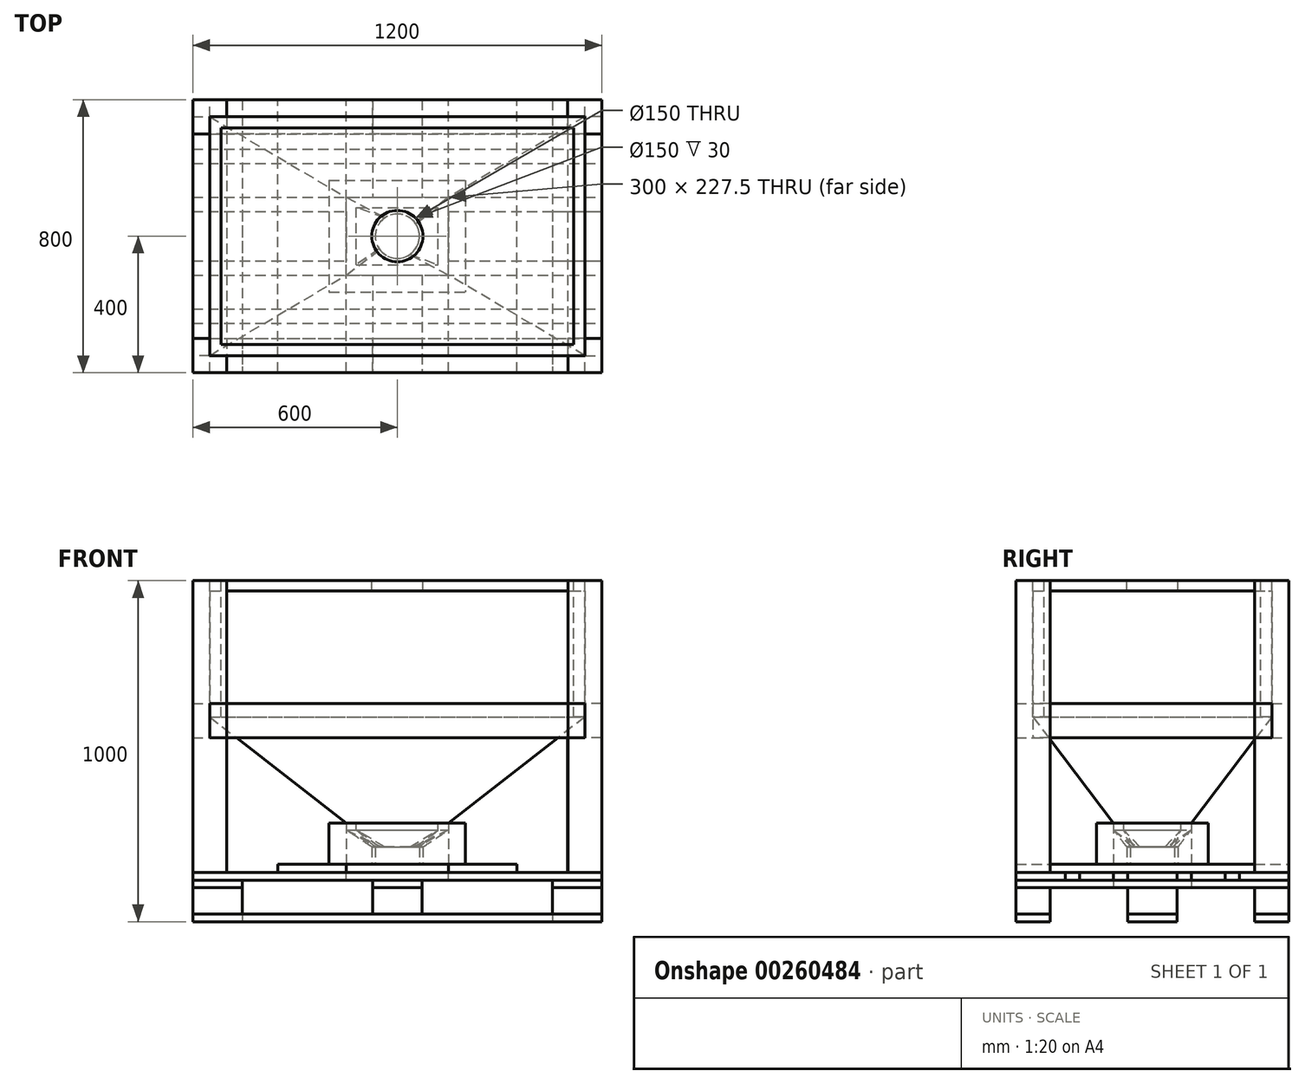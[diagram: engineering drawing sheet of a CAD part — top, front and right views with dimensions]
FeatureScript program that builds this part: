
annotation { "Feature Type Name" : "Feature", "Feature Type Description" : "" }
export const myFeature = defineFeature(function(context is Context, id is Id, definition is map)
    precondition{}
    {
        {
            var Q0;
            Q0=qCreatedBy(makeId("Top.planeOp"),FACE);
            var sketch = newSketch(context, id + "F0", { "sketchPlane" : qUnion([Q0])});
            skLineSegment(sketch, "E0.bottom", {"start": v(0, 800) * mm, "end": v(1200, 800) * mm});
            skLineSegment(sketch, "E0.top", {"start": v(0, 700) * mm, "end": v(1200, 700) * mm});
            skLineSegment(sketch, "E0.left", {"start": v(0, 800) * mm, "end": v(0, 700) * mm});
            skLineSegment(sketch, "E0.right", {"start": v(1200, 800) * mm, "end": v(1200, 700) * mm});
            skLineSegment(sketch, "E1.bottom", {"start": v(0, 100) * mm, "end": v(1200, 100) * mm});
            skLineSegment(sketch, "E1.top", {"start": v(0, 0) * mm, "end": v(1200, 0) * mm});
            skLineSegment(sketch, "E1.left", {"start": v(0, 100) * mm, "end": v(0, 0) * mm});
            skLineSegment(sketch, "E1.right", {"start": v(1200, 100) * mm, "end": v(1200, 0) * mm});
            skLineSegment(sketch, "E2.bottom", {"start": v(0, 472.5) * mm, "end": v(145, 472.5) * mm});
            skLineSegment(sketch, "E2.top", {"start": v(0, 327.5) * mm, "end": v(145, 327.5) * mm});
            skLineSegment(sketch, "E2.left", {"start": v(0, 472.5) * mm, "end": v(0, 327.5) * mm});
            skLineSegment(sketch, "E2.right", {"start": v(145, 472.5) * mm, "end": v(145, 327.5) * mm});
            skLineSegment(sketch, "E3.bottom", {"start": v(1055, 472.5) * mm, "end": v(1200, 472.5) * mm});
            skLineSegment(sketch, "E3.top", {"start": v(1055, 327.5) * mm, "end": v(1200, 327.5) * mm});
            skLineSegment(sketch, "E3.left", {"start": v(1055, 472.5) * mm, "end": v(1055, 327.5) * mm});
            skLineSegment(sketch, "E3.right", {"start": v(1200, 472.5) * mm, "end": v(1200, 327.5) * mm});
            skSolve(sketch);
        }
        {
            var Q0;
            Q0=qSketchRegion(id+"F0",true);
            extrude(context, id + "F1", {"entities" : qUnion([Q0]), "depth" : 22 * mm});
        }
        {
            var Q0;
            Q0=makeQuery(id+"F1.opExtrude","CAP_FACE",FACE,{"disambiguationData":[OSD([sQuery(id+"F0.wireOp",EDGE,"E1.bottom"),sQuery(id+"F0.wireOp",EDGE,"E1.top"),sQuery(id+"F0.wireOp",EDGE,"E1.left"),sQuery(id+"F0.wireOp",EDGE,"E1.right")])],"isStart":false});
            var sketch = newSketch(context, id + "F2", { "sketchPlane" : qUnion([Q0])});
            skLineSegment(sketch, "E4.0", {"start": v(0, 800) * mm, "end": v(0, 700) * mm});
            skLineSegment(sketch, "E5.0", {"start": v(1200, 800) * mm, "end": v(1200, 700) * mm});
            skLineSegment(sketch, "E6.0", {"start": v(1055, 472.5) * mm, "end": v(1200, 472.5) * mm});
            skLineSegment(sketch, "E7.0.0", {"start": v(1055, 472.5) * mm, "end": v(1055, 327.5) * mm});
            skLineSegment(sketch, "E7.0.1", {"start": v(1055, 327.5) * mm, "end": v(1200, 327.5) * mm});
            skLineSegment(sketch, "E7.0.2", {"start": v(1200, 327.5) * mm, "end": v(1200, 472.5) * mm});
            skLineSegment(sketch, "E7.0.3", {"start": v(1200, 472.5) * mm, "end": v(1055, 472.5) * mm});
            skLineSegment(sketch, "E8.0.0", {"start": v(0, 472.5) * mm, "end": v(0, 327.5) * mm});
            skLineSegment(sketch, "E8.0.1", {"start": v(0, 327.5) * mm, "end": v(145, 327.5) * mm});
            skLineSegment(sketch, "E8.0.2", {"start": v(145, 327.5) * mm, "end": v(145, 472.5) * mm});
            skLineSegment(sketch, "E8.0.3", {"start": v(145, 472.5) * mm, "end": v(0, 472.5) * mm});
            skPoint(sketch, "E9.0", {"position": v(0, 50) * mm});
            skLineSegment(sketch, "E10.0", {"start": v(0, 100) * mm, "end": v(0, 0) * mm});
            skLineSegment(sketch, "E11.0", {"start": v(1200, 100) * mm, "end": v(1200, 0) * mm});
            skLineSegment(sketch, "E12.bottom", {"start": v(0, 800) * mm, "end": v(145, 800) * mm});
            skLineSegment(sketch, "E12.top", {"start": v(0, 800) * mm, "end": v(145, 800) * mm});
            skLineSegment(sketch, "E12.left", {"start": v(0, 800) * mm, "end": v(0, 800) * mm});
            skLineSegment(sketch, "E12.right", {"start": v(145, 800) * mm, "end": v(145, 800) * mm});
            skLineSegment(sketch, "E13.bottom", {"start": v(1200, 800) * mm, "end": v(1055, 800) * mm});
            skLineSegment(sketch, "E13.top", {"start": v(1200, 800) * mm, "end": v(1055, 800) * mm});
            skLineSegment(sketch, "E13.left", {"start": v(1200, 800) * mm, "end": v(1200, 800) * mm});
            skLineSegment(sketch, "E13.right", {"start": v(1055, 800) * mm, "end": v(1055, 800) * mm});
            skLineSegment(sketch, "E14.bottom", {"start": v(1055, 800) * mm, "end": v(1200, 800) * mm});
            skLineSegment(sketch, "E14.top", {"start": v(1055, 700) * mm, "end": v(1200, 700) * mm});
            skLineSegment(sketch, "E14.left", {"start": v(1055, 800) * mm, "end": v(1055, 700) * mm});
            skLineSegment(sketch, "E15.bottom", {"start": v(1200, 100) * mm, "end": v(1055, 100) * mm});
            skLineSegment(sketch, "E15.top", {"start": v(1200, 100) * mm, "end": v(1055, 100) * mm});
            skLineSegment(sketch, "E15.left", {"start": v(1200, 100) * mm, "end": v(1200, 100) * mm});
            skLineSegment(sketch, "E15.right", {"start": v(1055, 100) * mm, "end": v(1055, 100) * mm});
            skLineSegment(sketch, "E16.bottom", {"start": v(1055, 100) * mm, "end": v(1200, 100) * mm});
            skLineSegment(sketch, "E16.top", {"start": v(1055, 0) * mm, "end": v(1200, 0) * mm});
            skLineSegment(sketch, "E16.left", {"start": v(1055, 100) * mm, "end": v(1055, 0) * mm});
            skLineSegment(sketch, "E17.bottom", {"start": v(0, 100) * mm, "end": v(145, 100) * mm});
            skLineSegment(sketch, "E17.top", {"start": v(0, 100) * mm, "end": v(145, 100) * mm});
            skLineSegment(sketch, "E17.left", {"start": v(0, 100) * mm, "end": v(0, 100) * mm});
            skLineSegment(sketch, "E17.right", {"start": v(145, 100) * mm, "end": v(145, 100) * mm});
            skLineSegment(sketch, "E18.bottom", {"start": v(145, 0) * mm, "end": v(0, 0) * mm});
            skLineSegment(sketch, "E18.top", {"start": v(145, 0) * mm, "end": v(0, 0) * mm});
            skLineSegment(sketch, "E18.left", {"start": v(145, 0) * mm, "end": v(145, 0) * mm});
            skLineSegment(sketch, "E18.right", {"start": v(0, 0) * mm, "end": v(0, 0) * mm});
            skLineSegment(sketch, "E19", {"start": v(145, 100) * mm, "end": v(145, 0) * mm});
            skLineSegment(sketch, "E20", {"start": v(145, 800) * mm, "end": v(145, 700) * mm});
            skLineSegment(sketch, "E21", {"start": v(145, 700) * mm, "end": v(0, 700) * mm});
            skLineSegment(sketch, "E22", {"start": v(527.5, 0) * mm, "end": v(527.5, 800) * mm, "construction": true});
            skLineSegment(sketch, "E23", {"start": v(672.5, 800) * mm, "end": v(672.5, 0) * mm, "construction": true});
            skLineSegment(sketch, "E24", {"start": v(527.5, 800) * mm, "end": v(672.5, 800) * mm});
            skLineSegment(sketch, "E25", {"start": v(672.5, 700) * mm, "end": v(527.5, 700) * mm});
            skLineSegment(sketch, "E26", {"start": v(527.5, 700) * mm, "end": v(527.5, 800) * mm});
            skLineSegment(sketch, "E27", {"start": v(527.5, 0) * mm, "end": v(527.5, 100) * mm});
            skLineSegment(sketch, "E28", {"start": v(527.5, 100) * mm, "end": v(672.5, 100) * mm});
            skLineSegment(sketch, "E29", {"start": v(672.5, 100) * mm, "end": v(672.5, 0) * mm});
            skLineSegment(sketch, "E30", {"start": v(527.5, 0) * mm, "end": v(672.5, 0) * mm});
            skLineSegment(sketch, "E31", {"start": v(672.5, 800) * mm, "end": v(672.5, 700) * mm});
            skSolve(sketch);
        }
        {
            var Q0;
            Q0=qSketchRegion(id+"F2",true);
            extrude(context, id + "F3", {"entities" : qUnion([Q0]), "depth" : 78 * mm});
        }
        {
            var Q0;
            Q0=makeQuery(id+"F3.opExtrude","CAP_FACE",FACE,{"disambiguationData":[OSD([sQuery(id+"F2.wireOp",EDGE,"E10.0"),sQuery(id+"F2.wireOp",EDGE,"E17.top"),sQuery(id+"F2.wireOp",EDGE,"E18.top"),sQuery(id+"F2.wireOp",EDGE,"E19")])],"isStart":false});
            var sketch = newSketch(context, id + "F4", { "sketchPlane" : qUnion([Q0])});
            skPoint(sketch, "E32.0", {"position": v(0, 800) * mm});
            skPoint(sketch, "E33.0", {"position": v(145, 0) * mm});
            skPoint(sketch, "E34.0", {"position": v(527.5, 800) * mm});
            skPoint(sketch, "E35.0", {"position": v(672.5, 0) * mm});
            skPoint(sketch, "E36.0", {"position": v(1055, 800) * mm});
            skPoint(sketch, "E37.0", {"position": v(1200, 0) * mm});
            skLineSegment(sketch, "E38.bottom", {"start": v(0, 800) * mm, "end": v(145, 800) * mm});
            skLineSegment(sketch, "E38.top", {"start": v(0, 0) * mm, "end": v(145, 0) * mm});
            skLineSegment(sketch, "E38.left", {"start": v(0, 800) * mm, "end": v(0, 0) * mm});
            skLineSegment(sketch, "E38.right", {"start": v(145, 800) * mm, "end": v(145, 0) * mm});
            skLineSegment(sketch, "E39.bottom", {"start": v(527.5, 800) * mm, "end": v(672.5, 800) * mm});
            skLineSegment(sketch, "E39.top", {"start": v(527.5, 0) * mm, "end": v(672.5, 0) * mm});
            skLineSegment(sketch, "E39.left", {"start": v(527.5, 800) * mm, "end": v(527.5, 0) * mm});
            skLineSegment(sketch, "E39.right", {"start": v(672.5, 800) * mm, "end": v(672.5, 0) * mm});
            skLineSegment(sketch, "E40.bottom", {"start": v(1055, 800) * mm, "end": v(1200, 800) * mm});
            skLineSegment(sketch, "E40.top", {"start": v(1055, 0) * mm, "end": v(1200, 0) * mm});
            skLineSegment(sketch, "E40.left", {"start": v(1055, 800) * mm, "end": v(1055, 0) * mm});
            skLineSegment(sketch, "E40.right", {"start": v(1200, 800) * mm, "end": v(1200, 0) * mm});
            skSolve(sketch);
        }
        {
            var Q0;
            Q0=qSketchRegion(id+"F4",true);
            extrude(context, id + "F5", {"entities" : qUnion([Q0]), "depth" : 22 * mm});
        }
        {
            var Q0;
            Q0=makeQuery(id+"F5.opExtrude","CAP_FACE",FACE,{"disambiguationData":[OSD([sQuery(id+"F4.wireOp",EDGE,"E38.bottom"),sQuery(id+"F4.wireOp",EDGE,"E38.top"),sQuery(id+"F4.wireOp",EDGE,"E38.left"),sQuery(id+"F4.wireOp",EDGE,"E38.right")])],"isStart":false});
            var sketch = newSketch(context, id + "F6", { "sketchPlane" : qUnion([Q0])});
            skLineSegment(sketch, "E41.bottom", {"start": v(0, 0) * mm, "end": v(1200, 0) * mm});
            skLineSegment(sketch, "E41.top", {"start": v(0, 145) * mm, "end": v(1200, 145) * mm});
            skLineSegment(sketch, "E41.left", {"start": v(0, 0) * mm, "end": v(0, 145) * mm});
            skLineSegment(sketch, "E41.right", {"start": v(1200, 0) * mm, "end": v(1200, 145) * mm});
            skLineSegment(sketch, "E42.bottom", {"start": v(0, 800) * mm, "end": v(1199.38, 800) * mm});
            skLineSegment(sketch, "E42.top", {"start": v(0, 655) * mm, "end": v(1199.38, 655) * mm});
            skLineSegment(sketch, "E42.left", {"start": v(0, 800) * mm, "end": v(0, 655) * mm});
            skLineSegment(sketch, "E42.right", {"start": v(1199.38, 800) * mm, "end": v(1199.38, 655) * mm});
            skLineSegment(sketch, "E43.bottom", {"start": v(0, 613.75) * mm, "end": v(1200, 613.75) * mm});
            skLineSegment(sketch, "E43.top", {"start": v(0, 513.75) * mm, "end": v(1200, 513.75) * mm});
            skLineSegment(sketch, "E43.left", {"start": v(0, 613.75) * mm, "end": v(0, 513.75) * mm});
            skLineSegment(sketch, "E43.right", {"start": v(1200, 613.75) * mm, "end": v(1200, 513.75) * mm});
            skLineSegment(sketch, "E44.bottom", {"start": v(0, 472.5) * mm, "end": v(1200, 472.5) * mm});
            skLineSegment(sketch, "E44.top", {"start": v(0, 327.5) * mm, "end": v(1200, 327.5) * mm});
            skLineSegment(sketch, "E44.left", {"start": v(0, 472.5) * mm, "end": v(0, 327.5) * mm});
            skLineSegment(sketch, "E44.right", {"start": v(1200, 472.5) * mm, "end": v(1200, 327.5) * mm});
            skLineSegment(sketch, "E45.bottom", {"start": v(0, 286.25) * mm, "end": v(1200, 286.25) * mm});
            skLineSegment(sketch, "E45.top", {"start": v(0, 186.25) * mm, "end": v(1200, 186.25) * mm});
            skLineSegment(sketch, "E45.left", {"start": v(0, 286.25) * mm, "end": v(0, 186.25) * mm});
            skLineSegment(sketch, "E45.right", {"start": v(1200, 286.25) * mm, "end": v(1200, 186.25) * mm});
            skLineSegment(sketch, "E46", {"start": v(0, 0) * mm, "end": v(0, 800) * mm, "construction": true});
            skLineSegment(sketch, "E47.0", {"start": v(1200, 800) * mm, "end": v(1200, 0) * mm, "construction": true});
            skSolve(sketch);
        }
        {
            var Q0;
            Q0=qSketchRegion(id+"F6",true);
            extrude(context, id + "F7", {"entities" : qUnion([Q0]), "depth" : 22 * mm});
        }
        {
            var Q0;
            Q0=makeQuery(id+"F7.opExtrude","CAP_FACE",FACE,{"disambiguationData":[OSD([sQuery(id+"F6.wireOp",EDGE,"E44.bottom"),sQuery(id+"F6.wireOp",EDGE,"E44.top"),sQuery(id+"F6.wireOp",EDGE,"E44.left"),sQuery(id+"F6.wireOp",EDGE,"E44.right")])],"isStart":false});
            var sketch = newSketch(context, id + "F8", { "sketchPlane" : qUnion([Q0])});
            skLineSegment(sketch, "E48.bottom", {"start": v(450, 513.75) * mm, "end": v(750, 513.75) * mm});
            skLineSegment(sketch, "E48.top", {"start": v(450, 286.25) * mm, "end": v(750, 286.25) * mm});
            skLineSegment(sketch, "E48.left", {"start": v(450, 513.75) * mm, "end": v(450, 286.25) * mm});
            skLineSegment(sketch, "E48.right", {"start": v(750, 513.75) * mm, "end": v(750, 286.25) * mm});
            skSolve(sketch);
        }
        {
            var Q0;
            {var subQ0=sQuery(id+"F8.wireOp",EDGE,"E48.bottom");Q0=makeQuery(id+"F8.imprint","IMPRINT",FACE,{"disambiguationData":[TD([[makeQuery(id+"F8.imprint","IMPRINT",EDGE,{"derivedFrom":subQ0}),-1.0]])]});}
            var Q1;
            {var subQ0=sQuery(id+"F8.wireOp",EDGE,"E48.left");var subQ1=makeQuery(id+"F7.opExtrude","CAP_EDGE",EDGE,{"disambiguationData":[OSD([sQuery(id+"F6.wireOp",EDGE,"E44.bottom")])],"isStart":false});var subQ2=makeQuery(id+"F8.imprint","INTERSECT",VERTEX,{"derivedFrom":[subQ1,subQ0]});Q1=makeQuery(id+"F8.imprint","IMPRINT",FACE,{"disambiguationData":[TD([[makeQuery(id+"F8.imprint","IMPRINT",EDGE,{"disambiguationData":[TD([[subQ2,-1.0]])],"derivedFrom":subQ0}),1.0]])]});}
            var Q2;
            {var subQ0=sQuery(id+"F8.wireOp",EDGE,"E48.top");Q2=makeQuery(id+"F8.imprint","IMPRINT",FACE,{"disambiguationData":[TD([[makeQuery(id+"F8.imprint","IMPRINT",EDGE,{"derivedFrom":subQ0}),1.0]])]});}
            extrude(context, id + "F9", {"entities" : qUnion([Q0, Q1, Q2]), "operationType" : NewBodyOperationType.REMOVE, "oppositeDirection" : true, "depth" : 288 * mm});
        }
        {
            var Q0;
            Q0=makeQuery(id+"F7.opExtrude","CAP_FACE",FACE,{"disambiguationData":[OSD([sQuery(id+"F6.wireOp",EDGE,"E41.bottom"),sQuery(id+"F6.wireOp",EDGE,"E41.top"),sQuery(id+"F6.wireOp",EDGE,"E41.left"),sQuery(id+"F6.wireOp",EDGE,"E41.right")])],"isStart":false});
            var sketch = newSketch(context, id + "F10", { "sketchPlane" : qUnion([Q0])});
            skLineSegment(sketch, "E49.0", {"start": v(450, 472.5) * mm, "end": v(450, 327.5) * mm});
            skLineSegment(sketch, "E50.0", {"start": v(750, 472.5) * mm, "end": v(750, 327.5) * mm});
            skLineSegment(sketch, "E51.bottom", {"start": v(450, 0) * mm, "end": v(250, 0) * mm});
            skLineSegment(sketch, "E51.top", {"start": v(450, 800) * mm, "end": v(250, 800) * mm});
            skLineSegment(sketch, "E51.left", {"start": v(450, 0) * mm, "end": v(450, 800) * mm});
            skLineSegment(sketch, "E51.right", {"start": v(250, 0) * mm, "end": v(250, 800) * mm});
            skLineSegment(sketch, "E52.bottom", {"start": v(750, 0) * mm, "end": v(950, 0) * mm});
            skLineSegment(sketch, "E52.top", {"start": v(750, 800) * mm, "end": v(950, 800) * mm});
            skLineSegment(sketch, "E52.left", {"start": v(750, 0) * mm, "end": v(750, 800) * mm});
            skLineSegment(sketch, "E52.right", {"start": v(950, 0) * mm, "end": v(950, 800) * mm});
            skSolve(sketch);
        }
        {
            var Q0;
            Q0 = qSketchRegion(id + "F10", true);
            extrude(context, id + "F11", {"entities" : qUnion([Q0]), "depth" : 25 * mm});
        }
        {
            var Q0;
            Q0=makeQuery(id+"F7.opExtrude","CAP_FACE",FACE,{"disambiguationData":[OSD([sQuery(id+"F6.wireOp",EDGE,"E41.bottom"),sQuery(id+"F6.wireOp",EDGE,"E41.top"),sQuery(id+"F6.wireOp",EDGE,"E41.left"),sQuery(id+"F6.wireOp",EDGE,"E41.right")])],"isStart":false});
            var sketch = newSketch(context, id + "F12", { "sketchPlane" : qUnion([Q0])});
            skPoint(sketch, "E53.0", {"position": v(0, 727.5) * mm});
            skLineSegment(sketch, "E54.bottom", {"start": v(0, 0) * mm, "end": v(100, 0) * mm});
            skLineSegment(sketch, "E55.bottom", {"start": v(1200, 0) * mm, "end": v(1100, 0) * mm});
            skLineSegment(sketch, "E56.bottom", {"start": v(1199.38, 800) * mm, "end": v(1099.38, 800) * mm});
            skLineSegment(sketch, "E56.right", {"start": v(1099.38, 800) * mm, "end": v(1099.38, 700) * mm});
            skLineSegment(sketch, "E57.bottom", {"start": v(0, 800) * mm, "end": v(100, 800) * mm});
            skLineSegment(sketch, "E58", {"start": v(1099.38, 700) * mm, "end": v(1199.38, 700) * mm});
            skLineSegment(sketch, "E59", {"start": v(1199.38, 700) * mm, "end": v(1199.38, 800) * mm});
            skLineSegment(sketch, "E60", {"start": v(100, 800) * mm, "end": v(100, 700) * mm});
            skLineSegment(sketch, "E61", {"start": v(100, 700) * mm, "end": v(0, 700) * mm});
            skLineSegment(sketch, "E62", {"start": v(0, 700) * mm, "end": v(0, 800) * mm});
            skLineSegment(sketch, "E63", {"start": v(0, 0) * mm, "end": v(0, 100) * mm});
            skLineSegment(sketch, "E64", {"start": v(0, 100) * mm, "end": v(100, 100) * mm});
            skLineSegment(sketch, "E65", {"start": v(100, 100) * mm, "end": v(100, 0) * mm});
            skLineSegment(sketch, "E66", {"start": v(1200, 0) * mm, "end": v(1200, 100) * mm});
            skLineSegment(sketch, "E67", {"start": v(1200, 100) * mm, "end": v(1100, 100) * mm});
            skLineSegment(sketch, "E68", {"start": v(1100, 100) * mm, "end": v(1100, 0) * mm});
            skSolve(sketch);
        }
        {
            var Q0;
            Q0 = qSketchRegion(id + "F12", true);
            extrude(context, id + "F13", {"entities" : qUnion([Q0]), "depth" : 856 * mm});
        }
        {
            var Q0;
            Q0=makeQuery(id+"F13.opExtrude","CAP_FACE",FACE,{"disambiguationData":[OSD([sQuery(id+"F12.wireOp",EDGE,"E54.bottom"),sQuery(id+"F12.wireOp",EDGE,"E63"),sQuery(id+"F12.wireOp",EDGE,"E64"),sQuery(id+"F12.wireOp",EDGE,"E65")])],"isStart":false});
            var sketch = newSketch(context, id + "F14", { "sketchPlane" : qUnion([Q0])});
            skLineSegment(sketch, "E69.bottom", {"start": v(100, 100) * mm, "end": v(50, 100) * mm});
            skLineSegment(sketch, "E69.top", {"start": v(100, 50) * mm, "end": v(50, 50) * mm});
            skLineSegment(sketch, "E69.left", {"start": v(100, 100) * mm, "end": v(100, 50) * mm});
            skLineSegment(sketch, "E69.right", {"start": v(50, 100) * mm, "end": v(50, 50) * mm});
            skLineSegment(sketch, "E70.bottom", {"start": v(100, 700) * mm, "end": v(50, 700) * mm});
            skLineSegment(sketch, "E70.top", {"start": v(100, 750) * mm, "end": v(50, 750) * mm});
            skLineSegment(sketch, "E70.left", {"start": v(100, 700) * mm, "end": v(100, 750) * mm});
            skLineSegment(sketch, "E70.right", {"start": v(50, 700) * mm, "end": v(50, 750) * mm});
            skLineSegment(sketch, "E71.bottom", {"start": v(1149.38, 750) * mm, "end": v(1099.38, 750) * mm});
            skLineSegment(sketch, "E71.top", {"start": v(1149.38, 700) * mm, "end": v(1099.38, 700) * mm});
            skLineSegment(sketch, "E71.left", {"start": v(1149.38, 750) * mm, "end": v(1149.38, 700) * mm});
            skLineSegment(sketch, "E71.right", {"start": v(1099.38, 750) * mm, "end": v(1099.38, 700) * mm});
            skLineSegment(sketch, "E72.bottom", {"start": v(1150, 50) * mm, "end": v(1100, 50) * mm});
            skLineSegment(sketch, "E72.top", {"start": v(1150, 100) * mm, "end": v(1100, 100) * mm});
            skLineSegment(sketch, "E72.left", {"start": v(1150, 50) * mm, "end": v(1150, 100) * mm});
            skLineSegment(sketch, "E72.right", {"start": v(1100, 50) * mm, "end": v(1100, 100) * mm});
            skSolve(sketch);
        }
        {
            var Q0;
            Q0 = qSketchRegion(id + "F14", true);
            extrude(context, id + "F15", {"entities" : qUnion([Q0]), "operationType" : NewBodyOperationType.REMOVE, "oppositeDirection" : true, "depth" : 400 * mm});
        }
        {
            var Q0;
            Q0=makeQuery(id+"F15.boolean.opBoolean","COPY",FACE,{"derivedFrom":makeQuery(id+"F15.opExtrude","CAP_FACE",FACE,{"disambiguationData":[OSD([sQuery(id+"F14.wireOp",EDGE,"E69.bottom"),sQuery(id+"F14.wireOp",EDGE,"E69.top"),sQuery(id+"F14.wireOp",EDGE,"E69.left"),sQuery(id+"F14.wireOp",EDGE,"E69.right")])],"isStart":false})});
            var sketch = newSketch(context, id + "F16", { "sketchPlane" : qUnion([Q0])});
            skLineSegment(sketch, "E73.bottom", {"start": v(50, 50) * mm, "end": v(1149.38, 50) * mm});
            skLineSegment(sketch, "E73.top", {"start": v(50, 750) * mm, "end": v(1149.38, 750) * mm});
            skLineSegment(sketch, "E73.left", {"start": v(50, 50) * mm, "end": v(50, 750) * mm});
            skLineSegment(sketch, "E73.right", {"start": v(1149.38, 50) * mm, "end": v(1149.38, 750) * mm});
            skSolve(sketch);
        }
        {
            var Q0;
            Q0 = qSketchRegion(id + "F16", true);
            extrude(context, id + "F17", {"entities" : qUnion([Q0]), "depth" : 400 * mm});
        }
        {
            var Q0;
            Q0=makeQuery(id+"F11.opExtrude","CAP_FACE",FACE,{"disambiguationData":[OSD([sQuery(id+"F10.wireOp",EDGE,"E52.bottom"),sQuery(id+"F10.wireOp",EDGE,"E52.top"),sQuery(id+"F10.wireOp",EDGE,"E52.left"),sQuery(id+"F10.wireOp",EDGE,"E52.right")])],"isStart":false});
            var sketch = newSketch(context, id + "F18", { "sketchPlane" : qUnion([Q0])});
            skCircle(sketch, "E74", {"center": v(600, 400) * mm, "radius": 75 * mm});
            skSolve(sketch);
        }
        {
            var Q0;
            Q0 = qSketchRegion(id + "F18", true);
            extrude(context, id + "F19", {"entities" : qUnion([Q0]), "depth" : 50 * mm});
        }
        {
            var Q0;
            Q0=makeQuery(id+"F19.opExtrude","CAP_FACE",FACE,{"disambiguationData":[OSD([sQuery(id+"F18.wireOp",EDGE,"E74"),sQuery(id+"F18.wireOp",EDGE,"d730c985-3c26-4322-8aea-f7a2ef2ff4ab.0")])],"isStart":false});
            cPlane(context, id + "F20", {"entities" : qUnion([Q0]), "cplaneType" : CPlaneType.OFFSET, "offset" : 50 * mm, "width" : 150 * mm, "height" : 150 * mm});
        }
        {
            var Q0;
            Q0=qCreatedBy(id+"F20.planeOp",FACE);
            var sketch = newSketch(context, id + "F21", { "sketchPlane" : qUnion([Q0])});
            skLineSegment(sketch, "E75.bottom", {"start": v(450, 286.25) * mm, "end": v(750, 286.25) * mm});
            skLineSegment(sketch, "E75.top", {"start": v(450, 513.75) * mm, "end": v(750, 513.75) * mm});
            skLineSegment(sketch, "E75.left", {"start": v(450, 286.25) * mm, "end": v(450, 513.75) * mm});
            skLineSegment(sketch, "E75.right", {"start": v(750, 286.25) * mm, "end": v(750, 513.75) * mm});
            skSolve(sketch);
        }
        {
            var Q0;
            Q0 = qSketchRegion(id + "F21", true);
            extrude(context, id + "F22", {"entities" : qUnion([Q0]), "depth" : 20 * mm});
        }
        {
            var Q1;
            Q1=makeQuery(id+"F22.opExtrude","CAP_FACE",FACE,{"disambiguationData":[OSD([sQuery(id+"F21.wireOp",EDGE,"E75.bottom"),sQuery(id+"F21.wireOp",EDGE,"E75.top"),sQuery(id+"F21.wireOp",EDGE,"E75.left"),sQuery(id+"F21.wireOp",EDGE,"E75.right")])],"isStart":true});
            var Q2;
            Q2=makeQuery(id+"F19.opExtrude","CAP_FACE",FACE,{"disambiguationData":[OSD([sQuery(id+"F18.wireOp",EDGE,"E74")])],"isStart":false});
            loft(context, id + "F23", {"operationType" : NewBodyOperationType.ADD, "sheetProfilesArray" : [{ "sheetProfileEntities" : qUnion([Q1]) }, { "sheetProfileEntities" : qUnion([Q2]) }]});
        }
        {
            var Q0;
            Q0=makeQuery(id+"F17.opExtrude","CAP_FACE",FACE,{"disambiguationData":[OSD([sQuery(id+"F16.wireOp",EDGE,"E73.bottom"),sQuery(id+"F16.wireOp",EDGE,"E73.top"),sQuery(id+"F16.wireOp",EDGE,"E73.left"),sQuery(id+"F16.wireOp",EDGE,"E73.right")])],"isStart":true});
            var Q1;
            Q1=makeQuery(id+"F22.opExtrude","CAP_FACE",FACE,{"disambiguationData":[OSD([sQuery(id+"F21.wireOp",EDGE,"E75.bottom"),sQuery(id+"F21.wireOp",EDGE,"E75.top"),sQuery(id+"F21.wireOp",EDGE,"E75.left"),sQuery(id+"F21.wireOp",EDGE,"E75.right")])],"isStart":false});
            loft(context, id + "F24", {"sheetProfilesArray" : [{ "sheetProfileEntities" : qUnion([Q0]) }, { "sheetProfileEntities" : qUnion([Q1]) }]});
        }
        {
            var Q0;
            Q0=makeQuery(id+"F17.opExtrude","CAP_FACE",FACE,{"disambiguationData":[OSD([sQuery(id+"F16.wireOp",EDGE,"E73.bottom"),sQuery(id+"F16.wireOp",EDGE,"E73.top"),sQuery(id+"F16.wireOp",EDGE,"E73.left"),sQuery(id+"F16.wireOp",EDGE,"E73.right")])],"isStart":false});
            var sketch = newSketch(context, id + "F25", { "sketchPlane" : qUnion([Q0])});
            skLineSegment(sketch, "E76.0", {"start": v(83, 83) * mm, "end": v(83, 717) * mm});
            skLineSegment(sketch, "E76.1", {"start": v(83, 83) * mm, "end": v(1116.38, 83) * mm});
            skLineSegment(sketch, "E76.2", {"start": v(1116.38, 83) * mm, "end": v(1116.38, 717) * mm});
            skLineSegment(sketch, "E76.3", {"start": v(83, 717) * mm, "end": v(1116.38, 717) * mm});
            skSolve(sketch);
        }
        {
            var Q0;
            Q0 = qSketchRegion(id + "F25", true);
            extrude(context, id + "F26", {"entities" : qUnion([Q0]), "oppositeDirection" : true, "depth" : 400 * mm});
        }
        {
            var Q0;
            Q0=makeQuery(id+"F19.opExtrude","CAP_FACE",FACE,{"disambiguationData":[OSD([sQuery(id+"F18.wireOp",EDGE,"E74")])],"isStart":true});
            var sketch = newSketch(context, id + "F27", { "sketchPlane" : qUnion([Q0])});
            skCircle(sketch, "E77.0", {"center": v(600, -400) * mm, "radius": 65 * mm});
            skSolve(sketch);
        }
        {
            var Q0;
            Q0=makeQuery(id+"F22.opExtrude","CAP_FACE",FACE,{"disambiguationData":[OSD([sQuery(id+"F21.wireOp",EDGE,"E75.bottom"),sQuery(id+"F21.wireOp",EDGE,"E75.top"),sQuery(id+"F21.wireOp",EDGE,"E75.left"),sQuery(id+"F21.wireOp",EDGE,"E75.right")])],"isStart":false});
            var sketch = newSketch(context, id + "F28", { "sketchPlane" : qUnion([Q0])});
            skLineSegment(sketch, "E78.0", {"start": v(480, 316.25) * mm, "end": v(480, 483.75) * mm});
            skLineSegment(sketch, "E78.1", {"start": v(480, 316.25) * mm, "end": v(720, 316.25) * mm});
            skLineSegment(sketch, "E78.2", {"start": v(720, 316.25) * mm, "end": v(720, 483.75) * mm});
            skLineSegment(sketch, "E78.3", {"start": v(480, 483.75) * mm, "end": v(720, 483.75) * mm});
            skSolve(sketch);
        }
        {
            var Q0;
            Q0 = qSketchRegion(id + "F27", true);
            extrude(context, id + "F29", {"entities" : qUnion([Q0]), "oppositeDirection" : true, "depth" : 50 * mm});
        }
        {
            var Q0;
            Q0 = qSketchRegion(id + "F28", true);
            extrude(context, id + "F30", {"entities" : qUnion([Q0]), "oppositeDirection" : true, "depth" : 20 * mm});
        }
        {
            var Q0;
            Q0=makeQuery(id+"F29.opExtrude","CAP_FACE",FACE,{"disambiguationData":[OSD([sQuery(id+"F27.wireOp",EDGE,"E77.0")])],"isStart":false});
            var Q1;
            Q1=makeQuery(id+"F30.opExtrude","CAP_FACE",FACE,{"disambiguationData":[OSD([sQuery(id+"F28.wireOp",EDGE,"E78.0"),sQuery(id+"F28.wireOp",EDGE,"E78.1"),sQuery(id+"F28.wireOp",EDGE,"E78.2"),sQuery(id+"F28.wireOp",EDGE,"E78.3")])],"isStart":false});
            loft(context, id + "F31", {"sheetProfilesArray" : [{ "sheetProfileEntities" : qUnion([Q0]) }, { "sheetProfileEntities" : qUnion([Q1]) }]});
        }
        {
            var Q0;
            Q0=makeQuery(id+"F26.opExtrude","CAP_FACE",FACE,{"disambiguationData":[OSD([sQuery(id+"F25.wireOp",EDGE,"E76.0"),sQuery(id+"F25.wireOp",EDGE,"E76.1"),sQuery(id+"F25.wireOp",EDGE,"E76.2"),sQuery(id+"F25.wireOp",EDGE,"E76.3")])],"isStart":false});
            var Q1;
            Q1=makeQuery(id+"F30.opExtrude","CAP_FACE",FACE,{"disambiguationData":[OSD([sQuery(id+"F28.wireOp",EDGE,"E78.0"),sQuery(id+"F28.wireOp",EDGE,"E78.1"),sQuery(id+"F28.wireOp",EDGE,"E78.2"),sQuery(id+"F28.wireOp",EDGE,"E78.3")])],"isStart":true});
            loft(context, id + "F32", {"sheetProfilesArray" : [{ "sheetProfileEntities" : qUnion([Q0]) }, { "sheetProfileEntities" : qUnion([Q1]) }]});
        }
        {
            var Q0;
            Q0=makeQuery(id+"F17.opExtrude","SWEPT_BODY",BODY,{"disambiguationData":[OSD([sQuery(id+"F16.wireOp",EDGE,"E73.bottom"),sQuery(id+"F16.wireOp",EDGE,"E73.top"),sQuery(id+"F16.wireOp",EDGE,"E73.left"),sQuery(id+"F16.wireOp",EDGE,"E73.right")])]});
            var Q1;
            Q1=makeQuery(id+"F13.opExtrude","SWEPT_BODY",BODY,{"disambiguationData":[OSD([sQuery(id+"F12.wireOp",EDGE,"E54.bottom"),sQuery(id+"F12.wireOp",EDGE,"E63"),sQuery(id+"F12.wireOp",EDGE,"E64"),sQuery(id+"F12.wireOp",EDGE,"E65")])]});
            var Q2;
            Q2=makeQuery(id+"F13.opExtrude","SWEPT_BODY",BODY,{"disambiguationData":[OSD([sQuery(id+"F12.wireOp",EDGE,"E57.bottom"),sQuery(id+"F12.wireOp",EDGE,"E60"),sQuery(id+"F12.wireOp",EDGE,"E61"),sQuery(id+"F12.wireOp",EDGE,"E62")])]});
            var Q3;
            Q3=makeQuery(id+"F13.opExtrude","SWEPT_BODY",BODY,{"disambiguationData":[OSD([sQuery(id+"F12.wireOp",EDGE,"E56.bottom"),sQuery(id+"F12.wireOp",EDGE,"E56.right"),sQuery(id+"F12.wireOp",EDGE,"E58"),sQuery(id+"F12.wireOp",EDGE,"E59")])]});
            var Q4;
            Q4=makeQuery(id+"F13.opExtrude","SWEPT_BODY",BODY,{"disambiguationData":[OSD([sQuery(id+"F12.wireOp",EDGE,"E55.bottom"),sQuery(id+"F12.wireOp",EDGE,"E66"),sQuery(id+"F12.wireOp",EDGE,"E67"),sQuery(id+"F12.wireOp",EDGE,"E68")])]});
            booleanBodies(context, id + "F33", {"operationType" : BooleanOperationType.SUBTRACTION, "tools" : qUnion([Q0]), "targets" : qUnion([Q1, Q2, Q3, Q4]), "keepTools" : true});
        }
        {
            var Q0;
            Q0=makeQuery(id+"F32.opLoft","SWEPT_BODY",BODY,{"disambiguationData":[OSD([sQuery(id+"F25.wireOp",EDGE,"E76.0"),sQuery(id+"F25.wireOp",EDGE,"E76.1"),sQuery(id+"F25.wireOp",EDGE,"E76.2"),sQuery(id+"F25.wireOp",EDGE,"E76.3"),sQuery(id+"F28.wireOp",EDGE,"E78.0"),sQuery(id+"F28.wireOp",EDGE,"E78.1"),sQuery(id+"F28.wireOp",EDGE,"E78.2"),sQuery(id+"F28.wireOp",EDGE,"E78.3")])]});
            var Q1;
            Q1=makeQuery(id+"F17.opExtrude","SWEPT_BODY",BODY,{"disambiguationData":[OSD([sQuery(id+"F16.wireOp",EDGE,"E73.bottom"),sQuery(id+"F16.wireOp",EDGE,"E73.top"),sQuery(id+"F16.wireOp",EDGE,"E73.left"),sQuery(id+"F16.wireOp",EDGE,"E73.right")])]});
            booleanBodies(context, id + "F34", {"operationType" : BooleanOperationType.SUBTRACTION, "tools" : qUnion([Q0]), "targets" : qUnion([Q1])});
        }
        {
            var Q0;
            Q0=makeQuery(id+"F17.opExtrude","CAP_FACE",FACE,{"disambiguationData":[OSD([sQuery(id+"F16.wireOp",EDGE,"E73.bottom"),sQuery(id+"F16.wireOp",EDGE,"E73.top"),sQuery(id+"F16.wireOp",EDGE,"E73.left"),sQuery(id+"F16.wireOp",EDGE,"E73.right")])],"isStart":false});
            var sketch = newSketch(context, id + "F35", { "sketchPlane" : qUnion([Q0])});
            skLineSegment(sketch, "E79.0", {"start": v(50, 50) * mm, "end": v(50, 750) * mm});
            skLineSegment(sketch, "E80.0", {"start": v(50, 750) * mm, "end": v(1149.38, 750) * mm});
            skLineSegment(sketch, "E81.0", {"start": v(1149.38, 50) * mm, "end": v(1149.38, 750) * mm});
            skLineSegment(sketch, "E82.0", {"start": v(50, 50) * mm, "end": v(1149.38, 50) * mm});
            skSolve(sketch);
        }
        {
            var Q0;
            Q0 = qSketchRegion(id + "F35", true);
            extrude(context, id + "F36", {"entities" : qUnion([Q0]), "oppositeDirection" : true, "depth" : 30 * mm});
        }
        {
            var Q0;
            Q0=makeQuery(id+"F36.opExtrude","SWEPT_BODY",BODY,{"disambiguationData":[OSD([sQuery(id+"F35.wireOp",EDGE,"E79.0"),sQuery(id+"F35.wireOp",EDGE,"E80.0"),sQuery(id+"F35.wireOp",EDGE,"E81.0"),sQuery(id+"F35.wireOp",EDGE,"E82.0")])]});
            var Q1;
            Q1=makeQuery(id+"F17.opExtrude","SWEPT_BODY",BODY,{"disambiguationData":[OSD([sQuery(id+"F16.wireOp",EDGE,"E73.bottom"),sQuery(id+"F16.wireOp",EDGE,"E73.top"),sQuery(id+"F16.wireOp",EDGE,"E73.left"),sQuery(id+"F16.wireOp",EDGE,"E73.right")])]});
            booleanBodies(context, id + "F37", {"operationType" : BooleanOperationType.SUBTRACTION, "tools" : qUnion([Q0]), "targets" : qUnion([Q1]), "keepTools" : true});
        }
        {
            var Q0;
            Q0=makeQuery(id+"F36.opExtrude","CAP_FACE",FACE,{"disambiguationData":[OSD([sQuery(id+"F35.wireOp",EDGE,"E79.0"),sQuery(id+"F35.wireOp",EDGE,"E80.0"),sQuery(id+"F35.wireOp",EDGE,"E81.0"),sQuery(id+"F35.wireOp",EDGE,"E82.0")])],"isStart":true});
            var sketch = newSketch(context, id + "F38", { "sketchPlane" : qUnion([Q0])});
            skCircle(sketch, "E83", {"center": v(600, 400) * mm, "radius": 75 * mm});
            skSolve(sketch);
        }
        {
            var Q0;
            Q0 = qSketchRegion(id + "F38", true);
            extrude(context, id + "F39", {"entities" : qUnion([Q0]), "operationType" : NewBodyOperationType.REMOVE, "oppositeDirection" : true, "depth" : 30 * mm});
        }
        {
            var Q0;
            Q0=qCreatedBy(id+"F20.planeOp",FACE);
            cPlane(context, id + "F40", {"entities" : qUnion([Q0]), "cplaneType" : CPlaneType.OFFSET, "offset" : 270 * mm, "width" : 150 * mm, "height" : 150 * mm});
        }
        {
            var Q0;
            Q0=qCreatedBy(id+"F40.planeOp",FACE);
            var sketch = newSketch(context, id + "F41", { "sketchPlane" : qUnion([Q0])});
            skLineSegment(sketch, "E84", {"start": v(0, 750) * mm, "end": v(50, 750) * mm});
            skLineSegment(sketch, "E85", {"start": v(50, 750) * mm, "end": v(50, 700) * mm});
            skLineSegment(sketch, "E86", {"start": v(50, 700) * mm, "end": v(100, 700) * mm});
            skLineSegment(sketch, "E87", {"start": v(100, 700) * mm, "end": v(100, 100) * mm});
            skLineSegment(sketch, "E88", {"start": v(100, 100) * mm, "end": v(50, 100) * mm});
            skLineSegment(sketch, "E89", {"start": v(50, 100) * mm, "end": v(50, 50) * mm});
            skLineSegment(sketch, "E90", {"start": v(50, 50) * mm, "end": v(0, 50) * mm});
            skLineSegment(sketch, "E91", {"start": v(0, 50) * mm, "end": v(0, 750) * mm});
            skLineSegment(sketch, "E92", {"start": v(1199.38, 750) * mm, "end": v(1149.38, 750) * mm});
            skLineSegment(sketch, "E93", {"start": v(1149.38, 750) * mm, "end": v(1149.38, 700) * mm});
            skLineSegment(sketch, "E94", {"start": v(1149.38, 700) * mm, "end": v(1099.38, 700) * mm});
            skLineSegment(sketch, "E95", {"start": v(1099.38, 700) * mm, "end": v(1099.38, 100) * mm});
            skLineSegment(sketch, "E96", {"start": v(1099.38, 100) * mm, "end": v(1149.38, 100) * mm});
            skLineSegment(sketch, "E97", {"start": v(1149.38, 100) * mm, "end": v(1149.38, 50) * mm});
            skLineSegment(sketch, "E98", {"start": v(1149.38, 50) * mm, "end": v(1199.38, 50) * mm});
            skLineSegment(sketch, "E99", {"start": v(1199.38, 50) * mm, "end": v(1199.38, 750) * mm});
            skSolve(sketch);
        }
        {
            var Q0;
            Q0 = qSketchRegion(id + "F41", true);
            extrude(context, id + "F42", {"entities" : qUnion([Q0]), "depth" : 100 * mm});
        }
        {
            var Q0;
            Q0=qCreatedBy(id+"F40.planeOp",FACE);
            var sketch = newSketch(context, id + "F43", { "sketchPlane" : qUnion([Q0])});
            skPoint(sketch, "E100.0", {"position": v(50, 750) * mm});
            skPoint(sketch, "E101.0", {"position": v(100, 700) * mm});
            skPoint(sketch, "E102.0", {"position": v(1149.38, 750) * mm});
            skPoint(sketch, "E103.0", {"position": v(1099.38, 700) * mm});
            skPoint(sketch, "E104.0", {"position": v(1099.38, 100) * mm});
            skPoint(sketch, "E105.0", {"position": v(1149.38, 50) * mm});
            skPoint(sketch, "E106.0", {"position": v(100, 100) * mm});
            skPoint(sketch, "E107.0", {"position": v(50, 50) * mm});
            skLineSegment(sketch, "E108", {"start": v(50, 750) * mm, "end": v(100, 750) * mm});
            skLineSegment(sketch, "E109", {"start": v(100, 750) * mm, "end": v(100, 700) * mm});
            skLineSegment(sketch, "E110", {"start": v(1099.38, 700) * mm, "end": v(100, 700) * mm});
            skLineSegment(sketch, "E111", {"start": v(1099.38, 700) * mm, "end": v(1099.38, 750) * mm});
            skLineSegment(sketch, "E112", {"start": v(1099.38, 750) * mm, "end": v(1149.38, 750) * mm});
            skLineSegment(sketch, "E113", {"start": v(1149.38, 750) * mm, "end": v(1149.38, 800) * mm});
            skLineSegment(sketch, "E114", {"start": v(1149.38, 800) * mm, "end": v(50, 800) * mm});
            skLineSegment(sketch, "E115", {"start": v(50, 750) * mm, "end": v(50, 800) * mm});
            skLineSegment(sketch, "E116", {"start": v(100, 100) * mm, "end": v(100, 50) * mm});
            skLineSegment(sketch, "E117", {"start": v(50, 50) * mm, "end": v(100, 50) * mm});
            skLineSegment(sketch, "E118", {"start": v(100, 100) * mm, "end": v(1099.38, 100) * mm});
            skLineSegment(sketch, "E119", {"start": v(1099.38, 100) * mm, "end": v(1099.38, 50) * mm});
            skLineSegment(sketch, "E120", {"start": v(1099.38, 50) * mm, "end": v(1149.38, 50) * mm});
            skLineSegment(sketch, "E121", {"start": v(1149.38, 0) * mm, "end": v(1149.38, 50) * mm});
            skLineSegment(sketch, "E122", {"start": v(1149.38, 0) * mm, "end": v(50, 0) * mm});
            skLineSegment(sketch, "E123", {"start": v(50, 0) * mm, "end": v(50, 50) * mm});
            skSolve(sketch);
        }
        {
            var Q0;
            Q0 = qSketchRegion(id + "F43", true);
            extrude(context, id + "F44", {"entities" : qUnion([Q0]), "depth" : 100 * mm});
        }
        {
            var Q0;
            Q0=makeQuery(id+"F11.opExtrude","CAP_FACE",FACE,{"disambiguationData":[OSD([sQuery(id+"F10.wireOp",EDGE,"E51.bottom"),sQuery(id+"F10.wireOp",EDGE,"E51.top"),sQuery(id+"F10.wireOp",EDGE,"E51.left"),sQuery(id+"F10.wireOp",EDGE,"E51.right")])],"isStart":false});
            var sketch = newSketch(context, id + "F45", { "sketchPlane" : qUnion([Q0])});
            skLineSegment(sketch, "E124.bottom", {"start": v(450, 513.75) * mm, "end": v(750, 513.75) * mm});
            skLineSegment(sketch, "E124.top", {"start": v(450, 286.25) * mm, "end": v(750, 286.25) * mm});
            skLineSegment(sketch, "E124.left", {"start": v(450, 513.75) * mm, "end": v(450, 286.25) * mm});
            skLineSegment(sketch, "E124.right", {"start": v(750, 513.75) * mm, "end": v(750, 286.25) * mm});
            skLineSegment(sketch, "E125.0", {"start": v(400, 563.75) * mm, "end": v(800, 563.75) * mm});
            skLineSegment(sketch, "E125.1", {"start": v(400, 563.75) * mm, "end": v(400, 236.25) * mm});
            skLineSegment(sketch, "E125.2", {"start": v(400, 236.25) * mm, "end": v(800, 236.25) * mm});
            skLineSegment(sketch, "E125.3", {"start": v(800, 563.75) * mm, "end": v(800, 236.25) * mm});
            skSolve(sketch);
        }
        {
            var Q0;
            Q0 = qSketchRegion(id + "F45", true);
            extrude(context, id + "F46", {"entities" : qUnion([Q0]), "depth" : 120 * mm});
        }
    });
